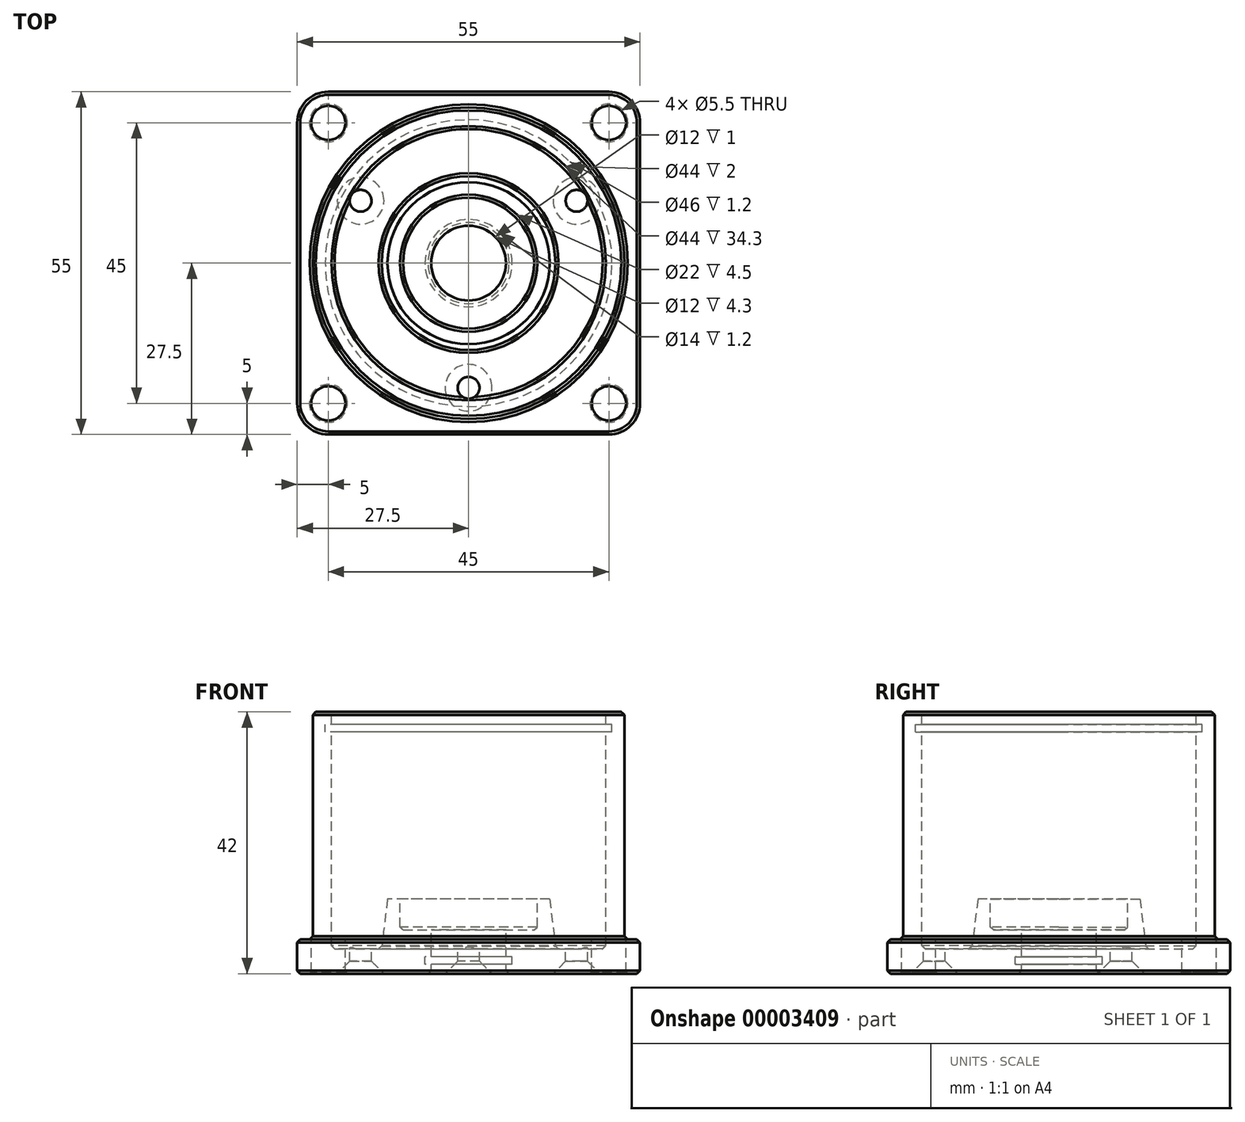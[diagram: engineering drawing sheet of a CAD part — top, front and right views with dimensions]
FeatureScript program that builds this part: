
annotation { "Feature Type Name" : "Feature", "Feature Type Description" : "" }
export const myFeature = defineFeature(function(context is Context, id is Id, definition is map)
    precondition{}
    {
        {
            var Q0;
            Q0=qCreatedBy(makeId("Top.planeOp"),FACE);
            var sketch = newSketch(context, id + "F0", { "sketchPlane" : qUnion([Q0])});
            skLineSegment(sketch, "E0.rect.bottom", {"start": v(-22.5, -27.5) * mm, "end": v(22.5, -27.5) * mm});
            skLineSegment(sketch, "E0.rect.top", {"start": v(-22.5, 27.5) * mm, "end": v(22.5, 27.5) * mm});
            skLineSegment(sketch, "E0.rect.left", {"start": v(-27.5, -22.5) * mm, "end": v(-27.5, 22.5) * mm});
            skLineSegment(sketch, "E0.rect.right", {"start": v(27.5, -22.5) * mm, "end": v(27.5, 22.5) * mm});
            skPoint(sketch, "E0.rect.middle", {"position": v(0, 0) * mm});
            skPoint(sketch, "E1.visualSharp", {"position": v(-27.5, 27.5) * mm});
            skArc(sketch, "E1.filletArc", {"start": v(-22.5, 27.5) * mm, "mid": v(-26.04, 26.04) * mm, "end": v(-27.5, 22.5) * mm});
            skPoint(sketch, "E2.visualSharp", {"position": v(27.5, 27.5) * mm});
            skArc(sketch, "E2.filletArc", {"start": v(27.5, 22.5) * mm, "mid": v(26.04, 26.04) * mm, "end": v(22.5, 27.5) * mm});
            skPoint(sketch, "E3.visualSharp", {"position": v(27.5, -27.5) * mm});
            skArc(sketch, "E3.filletArc", {"start": v(22.5, -27.5) * mm, "mid": v(26.04, -26.04) * mm, "end": v(27.5, -22.5) * mm});
            skPoint(sketch, "E4.visualSharp", {"position": v(-27.5, -27.5) * mm});
            skArc(sketch, "E4.filletArc", {"start": v(-27.5, -22.5) * mm, "mid": v(-26.04, -26.04) * mm, "end": v(-22.5, -27.5) * mm});
            skSolve(sketch);
        }
        {
            var Q0;
            Q0=makeQuery(id+"F0.imprint","IMPRINT",FACE,{"disambiguationData":[TD([[makeQuery(id+"F0.imprint","IMPRINT",EDGE,{"derivedFrom":sQuery(id+"F0.wireOp",EDGE,"E0.rect.bottom")}),1.0]])]});
            extrude(context, id + "F1", {"entities" : qUnion([Q0]), "depth" : 42 * mm});
        }
        {
            var Q0;
            Q0=qCreatedBy(makeId("Right.planeOp"),FACE);
            var sketch = newSketch(context, id + "F2", { "sketchPlane" : qUnion([Q0])});
            skLineSegment(sketch, "E5", {"start": v(-43.6, 5.5) * mm, "end": v(-25, 5.5) * mm});
            skLineSegment(sketch, "E6", {"start": v(-25, 5.5) * mm, "end": v(-25, 44.38) * mm});
            skLineSegment(sketch, "E7", {"start": v(-25, 44.38) * mm, "end": v(-22, 44.38) * mm});
            skLineSegment(sketch, "E8", {"start": v(-22, 44.38) * mm, "end": v(-22, 40) * mm});
            skLineSegment(sketch, "E9", {"start": v(-22, 40) * mm, "end": v(-23, 40) * mm});
            skLineSegment(sketch, "E10", {"start": v(-23, 40) * mm, "end": v(-23, 38.8) * mm});
            skLineSegment(sketch, "E11", {"start": v(-23, 38.8) * mm, "end": v(-22, 38.8) * mm});
            skLineSegment(sketch, "E12", {"start": v(-22, 38.8) * mm, "end": v(-22, 4) * mm});
            skLineSegment(sketch, "E13", {"start": v(-22, 4) * mm, "end": v(-13.98, 4) * mm});
            skLineSegment(sketch, "E14", {"start": v(-13.98, 4) * mm, "end": v(-13, 12) * mm});
            skLineSegment(sketch, "E15", {"start": v(-13, 12) * mm, "end": v(-11, 12) * mm});
            skLineSegment(sketch, "E16", {"start": v(-6, 12) * mm, "end": v(-6, 12) * mm});
            skLineSegment(sketch, "E17", {"start": v(-6, -1.43) * mm, "end": v(0, -1.43) * mm});
            skLineSegment(sketch, "E18", {"start": v(0, -1.43) * mm, "end": v(0, 48.79) * mm});
            skLineSegment(sketch, "E19", {"start": v(0, 48.79) * mm, "end": v(-43.6, 48.79) * mm});
            skLineSegment(sketch, "E20", {"start": v(-43.6, 48.79) * mm, "end": v(-43.6, 5.5) * mm});
            skLineSegment(sketch, "E21", {"start": v(-6, 2.7) * mm, "end": v(-6, 2.7) * mm});
            skLineSegment(sketch, "E22", {"start": v(-7, 2.7) * mm, "end": v(-7, 1.5) * mm});
            skLineSegment(sketch, "E23", {"start": v(-7, 1.5) * mm, "end": v(-6, 1.5) * mm});
            skLineSegment(sketch, "E24", {"start": v(-6, 1.5) * mm, "end": v(-6, -1.43) * mm});
            skLineSegment(sketch, "E25", {"start": v(-6, 2.7) * mm, "end": v(-7, 2.7) * mm});
            skLineSegment(sketch, "E26", {"start": v(-6, 7) * mm, "end": v(-6, 2.7) * mm});
            skLineSegment(sketch, "E27", {"start": v(-11, 12) * mm, "end": v(-11, 7) * mm});
            skLineSegment(sketch, "E28", {"start": v(-11, 7) * mm, "end": v(-6, 7) * mm});
            skSolve(sketch);
        }
        {
            var Q0;
            Q0=makeQuery(id+"F2.imprint","IMPRINT",FACE,{"disambiguationData":[TD([[makeQuery(id+"F2.imprint","IMPRINT",EDGE,{"derivedFrom":sQuery(id+"F2.wireOp",EDGE,"E5")}),1.0]])]});
            var Q1;
            Q1=sQuery(id+"F2.wireOp",EDGE,"E18");
            revolve(context, id + "F3", {"operationType" : NewBodyOperationType.REMOVE, "entities" : qUnion([Q0]), "axis" : qUnion([Q1]), "revolveType" : RevolveType.FULL, "oppositeDirection" : true});
        }
        {
            var Q0;
            Q0=makeQuery(id+"F3.boolean.opBoolean","INTERSECT",EDGE,{"derivedFrom":[makeQuery(id+"F1.opExtrude","CAP_FACE",FACE,{"disambiguationData":[OSD([sQuery(id+"F0.wireOp",EDGE,"E0.rect.bottom"),sQuery(id+"F0.wireOp",EDGE,"E0.rect.top"),sQuery(id+"F0.wireOp",EDGE,"E0.rect.left"),sQuery(id+"F0.wireOp",EDGE,"E0.rect.right"),sQuery(id+"F0.wireOp",EDGE,"E1.filletArc"),sQuery(id+"F0.wireOp",EDGE,"E2.filletArc"),sQuery(id+"F0.wireOp",EDGE,"E3.filletArc"),sQuery(id+"F0.wireOp",EDGE,"E4.filletArc")])],"isStart":true}),makeQuery(id+"F3.opRevolve","SWEPT_FACE",FACE,{"disambiguationData":[OSD([sQuery(id+"F2.wireOp",EDGE,"E24")])]})]});
            var Q1;
            Q1=makeQuery(id+"F1.opExtrude","CAP_FACE",FACE,{"disambiguationData":[OSD([sQuery(id+"F0.wireOp",EDGE,"E0.rect.bottom"),sQuery(id+"F0.wireOp",EDGE,"E0.rect.top"),sQuery(id+"F0.wireOp",EDGE,"E0.rect.left"),sQuery(id+"F0.wireOp",EDGE,"E0.rect.right"),sQuery(id+"F0.wireOp",EDGE,"E1.filletArc"),sQuery(id+"F0.wireOp",EDGE,"E2.filletArc"),sQuery(id+"F0.wireOp",EDGE,"E3.filletArc"),sQuery(id+"F0.wireOp",EDGE,"E4.filletArc")])],"isStart":true});
            var Q2;
            Q2=makeQuery(id+"F3.boolean.opBoolean","COPY",FACE,{"derivedFrom":makeQuery(id+"F3.opRevolve","SWEPT_FACE",FACE,{"disambiguationData":[OSD([sQuery(id+"F2.wireOp",EDGE,"E5")])]})});
            var Q3;
            Q3=makeQuery(id+"F3.boolean.opBoolean","INTERSECT",EDGE,{"derivedFrom":[makeQuery(id+"F1.opExtrude","CAP_FACE",FACE,{"disambiguationData":[OSD([sQuery(id+"F0.wireOp",EDGE,"E0.rect.bottom"),sQuery(id+"F0.wireOp",EDGE,"E0.rect.top"),sQuery(id+"F0.wireOp",EDGE,"E0.rect.left"),sQuery(id+"F0.wireOp",EDGE,"E0.rect.right"),sQuery(id+"F0.wireOp",EDGE,"E1.filletArc"),sQuery(id+"F0.wireOp",EDGE,"E2.filletArc"),sQuery(id+"F0.wireOp",EDGE,"E3.filletArc"),sQuery(id+"F0.wireOp",EDGE,"E4.filletArc")])],"isStart":false}),makeQuery(id+"F3.opRevolve","SWEPT_FACE",FACE,{"disambiguationData":[OSD([sQuery(id+"F2.wireOp",EDGE,"E6")])]})]});
            var Q4;
            Q4=makeQuery(id+"F3.boolean.opBoolean","COPY",EDGE,{"derivedFrom":makeQuery(id+"F3.opRevolve","SWEPT_EDGE",EDGE,{"disambiguationData":[OSD([sQuery(id+"F2.wireOp",EDGE,"E12"),sQuery(id+"F2.wireOp",EDGE,"E13")])]})});
            var Q5;
            Q5=makeQuery(id+"F3.boolean.opBoolean","COPY",EDGE,{"derivedFrom":makeQuery(id+"F3.opRevolve","SWEPT_EDGE",EDGE,{"disambiguationData":[OSD([sQuery(id+"F2.wireOp",EDGE,"E13"),sQuery(id+"F2.wireOp",EDGE,"E14")])]})});
            var Q6;
            Q6=makeQuery(id+"F3.boolean.opBoolean","COPY",EDGE,{"derivedFrom":makeQuery(id+"F3.opRevolve","SWEPT_EDGE",EDGE,{"disambiguationData":[OSD([sQuery(id+"F2.wireOp",EDGE,"E27"),sQuery(id+"F2.wireOp",EDGE,"E28")])]})});
            chamfer(context, id + "F4", {"entities" : qUnion([Q0, Q1, Q2, Q3, Q4, Q5, Q6]), "width" : 0.5 * mm, "tangentPropagation" : true});
        }
        {
            var Q0;
            Q0=makeQuery(id+"F3.boolean.opBoolean","COPY",FACE,{"derivedFrom":makeQuery(id+"F3.opRevolve","SWEPT_FACE",FACE,{"disambiguationData":[OSD([sQuery(id+"F2.wireOp",EDGE,"E5")])]})});
            var sketch = newSketch(context, id + "F5", { "sketchPlane" : qUnion([Q0])});
            skCircle(sketch, "E29", {"center": v(-22.5, 22.5) * mm, "radius": 2.75 * mm});
            skCircle(sketch, "E30", {"center": v(22.5, 22.5) * mm, "radius": 2.75 * mm});
            skCircle(sketch, "E31", {"center": v(22.5, -22.5) * mm, "radius": 2.75 * mm});
            skCircle(sketch, "E32", {"center": v(-22.5, -22.5) * mm, "radius": 2.75 * mm});
            skCircle(sketch, "E33", {"center": v(0, -20) * mm, "radius": 1.75 * mm});
            skSolve(sketch);
        }
        {
            var Q0;
            Q0=makeQuery(id+"F5.imprint","IMPRINT",FACE,{"disambiguationData":[TD([[makeQuery(id+"F5.imprint","IMPRINT",EDGE,{"derivedFrom":sQuery(id+"F5.wireOp",EDGE,"E29")}),1.0]])]});
            var Q1;
            Q1=makeQuery(id+"F5.imprint","IMPRINT",FACE,{"disambiguationData":[TD([[makeQuery(id+"F5.imprint","IMPRINT",EDGE,{"derivedFrom":sQuery(id+"F5.wireOp",EDGE,"E30")}),1.0]])]});
            var Q2;
            Q2=makeQuery(id+"F5.imprint","IMPRINT",FACE,{"disambiguationData":[TD([[makeQuery(id+"F5.imprint","IMPRINT",EDGE,{"derivedFrom":sQuery(id+"F5.wireOp",EDGE,"E31")}),1.0]])]});
            var Q3;
            Q3=makeQuery(id+"F5.imprint","IMPRINT",FACE,{"disambiguationData":[TD([[makeQuery(id+"F5.imprint","IMPRINT",EDGE,{"derivedFrom":sQuery(id+"F5.wireOp",EDGE,"E32")}),1.0]])]});
            extrude(context, id + "F6", {"entities" : qUnion([Q0, Q1, Q2, Q3]), "operationType" : NewBodyOperationType.REMOVE, "oppositeDirection" : true, "depth" : 8 * mm});
        }
        {
            var Q0;
            Q0=makeQuery(id+"F6.boolean.opBoolean","INTERSECT",EDGE,{"derivedFrom":[makeQuery(id+"F1.opExtrude","CAP_FACE",FACE,{"disambiguationData":[OSD([sQuery(id+"F0.wireOp",EDGE,"E0.rect.bottom"),sQuery(id+"F0.wireOp",EDGE,"E0.rect.top"),sQuery(id+"F0.wireOp",EDGE,"E0.rect.left"),sQuery(id+"F0.wireOp",EDGE,"E0.rect.right"),sQuery(id+"F0.wireOp",EDGE,"E1.filletArc"),sQuery(id+"F0.wireOp",EDGE,"E2.filletArc"),sQuery(id+"F0.wireOp",EDGE,"E3.filletArc"),sQuery(id+"F0.wireOp",EDGE,"E4.filletArc")])],"isStart":true}),makeQuery(id+"F6.opExtrude","SWEPT_FACE",FACE,{"disambiguationData":[OSD([sQuery(id+"F5.wireOp",EDGE,"E30")])]})]});
            var Q1;
            Q1=makeQuery(id+"F6.boolean.opBoolean","INTERSECT",EDGE,{"derivedFrom":[makeQuery(id+"F1.opExtrude","CAP_FACE",FACE,{"disambiguationData":[OSD([sQuery(id+"F0.wireOp",EDGE,"E0.rect.bottom"),sQuery(id+"F0.wireOp",EDGE,"E0.rect.top"),sQuery(id+"F0.wireOp",EDGE,"E0.rect.left"),sQuery(id+"F0.wireOp",EDGE,"E0.rect.right"),sQuery(id+"F0.wireOp",EDGE,"E1.filletArc"),sQuery(id+"F0.wireOp",EDGE,"E2.filletArc"),sQuery(id+"F0.wireOp",EDGE,"E3.filletArc"),sQuery(id+"F0.wireOp",EDGE,"E4.filletArc")])],"isStart":true}),makeQuery(id+"F6.opExtrude","SWEPT_FACE",FACE,{"disambiguationData":[OSD([sQuery(id+"F5.wireOp",EDGE,"E29")])]})]});
            var Q2;
            Q2=makeQuery(id+"F6.boolean.opBoolean","INTERSECT",EDGE,{"derivedFrom":[makeQuery(id+"F1.opExtrude","CAP_FACE",FACE,{"disambiguationData":[OSD([sQuery(id+"F0.wireOp",EDGE,"E0.rect.bottom"),sQuery(id+"F0.wireOp",EDGE,"E0.rect.top"),sQuery(id+"F0.wireOp",EDGE,"E0.rect.left"),sQuery(id+"F0.wireOp",EDGE,"E0.rect.right"),sQuery(id+"F0.wireOp",EDGE,"E1.filletArc"),sQuery(id+"F0.wireOp",EDGE,"E2.filletArc"),sQuery(id+"F0.wireOp",EDGE,"E3.filletArc"),sQuery(id+"F0.wireOp",EDGE,"E4.filletArc")])],"isStart":true}),makeQuery(id+"F6.opExtrude","SWEPT_FACE",FACE,{"disambiguationData":[OSD([sQuery(id+"F5.wireOp",EDGE,"E32")])]})]});
            var Q3;
            Q3=makeQuery(id+"F6.boolean.opBoolean","INTERSECT",EDGE,{"derivedFrom":[makeQuery(id+"F1.opExtrude","CAP_FACE",FACE,{"disambiguationData":[OSD([sQuery(id+"F0.wireOp",EDGE,"E0.rect.bottom"),sQuery(id+"F0.wireOp",EDGE,"E0.rect.top"),sQuery(id+"F0.wireOp",EDGE,"E0.rect.left"),sQuery(id+"F0.wireOp",EDGE,"E0.rect.right"),sQuery(id+"F0.wireOp",EDGE,"E1.filletArc"),sQuery(id+"F0.wireOp",EDGE,"E2.filletArc"),sQuery(id+"F0.wireOp",EDGE,"E3.filletArc"),sQuery(id+"F0.wireOp",EDGE,"E4.filletArc")])],"isStart":true}),makeQuery(id+"F6.opExtrude","SWEPT_FACE",FACE,{"disambiguationData":[OSD([sQuery(id+"F5.wireOp",EDGE,"E31")])]})]});
            var Q4;
            Q4=makeQuery(id+"F6.boolean.opBoolean","COPY",EDGE,{"derivedFrom":makeQuery(id+"F6.opExtrude","CAP_EDGE",EDGE,{"disambiguationData":[OSD([sQuery(id+"F5.wireOp",EDGE,"E32")])],"isStart":true})});
            var Q5;
            Q5=makeQuery(id+"F6.boolean.opBoolean","COPY",EDGE,{"derivedFrom":makeQuery(id+"F6.opExtrude","CAP_EDGE",EDGE,{"disambiguationData":[OSD([sQuery(id+"F5.wireOp",EDGE,"E29")])],"isStart":true})});
            var Q6;
            Q6=makeQuery(id+"F6.boolean.opBoolean","COPY",EDGE,{"derivedFrom":makeQuery(id+"F6.opExtrude","CAP_EDGE",EDGE,{"disambiguationData":[OSD([sQuery(id+"F5.wireOp",EDGE,"E30")])],"isStart":true})});
            var Q7;
            Q7=makeQuery(id+"F6.boolean.opBoolean","COPY",EDGE,{"derivedFrom":makeQuery(id+"F6.opExtrude","CAP_EDGE",EDGE,{"disambiguationData":[OSD([sQuery(id+"F5.wireOp",EDGE,"E31")])],"isStart":true})});
            chamfer(context, id + "F7", {"entities" : qUnion([Q0, Q1, Q2, Q3, Q4, Q5, Q6, Q7]), "width" : 0.3 * mm, "tangentPropagation" : true});
        }
        {
            var Q0;
            Q0=makeQuery(id+"F5.imprint","IMPRINT",FACE,{"disambiguationData":[TD([[makeQuery(id+"F5.imprint","IMPRINT",EDGE,{"derivedFrom":sQuery(id+"F5.wireOp",EDGE,"E33")}),1.0]])]});
            extrude(context, id + "F8", {"entities" : qUnion([Q0]), "operationType" : NewBodyOperationType.REMOVE, "oppositeDirection" : true, "depth" : 6 * mm});
        }
        {
            var Q0;
            Q0=makeQuery(id+"F8.boolean.opBoolean","COPY",FACE,{"derivedFrom":makeQuery(id+"F8.opExtrude","SWEPT_FACE",FACE,{"disambiguationData":[OSD([sQuery(id+"F5.wireOp",EDGE,"E33")])]})});
            var Q1;
            Q1=makeQuery(id+"F3.boolean.opBoolean","COPY",FACE,{"derivedFrom":makeQuery(id+"F3.opRevolve","SWEPT_FACE",FACE,{"disambiguationData":[OSD([sQuery(id+"F2.wireOp",EDGE,"E26")])]})});
            circularPattern(context, id + "F9", {"faces" : qUnion([Q0]), "axis" : qUnion([Q1]), "angle" : 120 * degree, "instanceCount" : 3, "patternType" : PatternType.FACE});
        }
        {
            var Q0;
            Q0=makeQuery(id+"F9.opPattern","COPY",EDGE,{"derivedFrom":makeQuery(id+"F8.boolean.opBoolean","INTERSECT",EDGE,{"derivedFrom":[makeQuery(id+"F1.opExtrude","CAP_FACE",FACE,{"disambiguationData":[OSD([sQuery(id+"F0.wireOp",EDGE,"E0.rect.bottom"),sQuery(id+"F0.wireOp",EDGE,"E0.rect.top"),sQuery(id+"F0.wireOp",EDGE,"E0.rect.left"),sQuery(id+"F0.wireOp",EDGE,"E0.rect.right"),sQuery(id+"F0.wireOp",EDGE,"E1.filletArc"),sQuery(id+"F0.wireOp",EDGE,"E2.filletArc"),sQuery(id+"F0.wireOp",EDGE,"E3.filletArc"),sQuery(id+"F0.wireOp",EDGE,"E4.filletArc")])],"isStart":true}),makeQuery(id+"F8.opExtrude","SWEPT_FACE",FACE,{"disambiguationData":[OSD([sQuery(id+"F5.wireOp",EDGE,"E33")])]})]}),"instanceName":"1"});
            var Q1;
            Q1=makeQuery(id+"F9.opPattern","COPY",EDGE,{"derivedFrom":makeQuery(id+"F8.boolean.opBoolean","INTERSECT",EDGE,{"derivedFrom":[makeQuery(id+"F1.opExtrude","CAP_FACE",FACE,{"disambiguationData":[OSD([sQuery(id+"F0.wireOp",EDGE,"E0.rect.bottom"),sQuery(id+"F0.wireOp",EDGE,"E0.rect.top"),sQuery(id+"F0.wireOp",EDGE,"E0.rect.left"),sQuery(id+"F0.wireOp",EDGE,"E0.rect.right"),sQuery(id+"F0.wireOp",EDGE,"E1.filletArc"),sQuery(id+"F0.wireOp",EDGE,"E2.filletArc"),sQuery(id+"F0.wireOp",EDGE,"E3.filletArc"),sQuery(id+"F0.wireOp",EDGE,"E4.filletArc")])],"isStart":true}),makeQuery(id+"F8.opExtrude","SWEPT_FACE",FACE,{"disambiguationData":[OSD([sQuery(id+"F5.wireOp",EDGE,"E33")])]})]}),"instanceName":"2"});
            var Q2;
            Q2=makeQuery(id+"F8.boolean.opBoolean","INTERSECT",EDGE,{"derivedFrom":[makeQuery(id+"F1.opExtrude","CAP_FACE",FACE,{"disambiguationData":[OSD([sQuery(id+"F0.wireOp",EDGE,"E0.rect.bottom"),sQuery(id+"F0.wireOp",EDGE,"E0.rect.top"),sQuery(id+"F0.wireOp",EDGE,"E0.rect.left"),sQuery(id+"F0.wireOp",EDGE,"E0.rect.right"),sQuery(id+"F0.wireOp",EDGE,"E1.filletArc"),sQuery(id+"F0.wireOp",EDGE,"E2.filletArc"),sQuery(id+"F0.wireOp",EDGE,"E3.filletArc"),sQuery(id+"F0.wireOp",EDGE,"E4.filletArc")])],"isStart":true}),makeQuery(id+"F8.opExtrude","SWEPT_FACE",FACE,{"disambiguationData":[OSD([sQuery(id+"F5.wireOp",EDGE,"E33")])]})]});
            chamfer(context, id + "F10", {"entities" : qUnion([Q0, Q1, Q2]), "width" : 2 * mm, "tangentPropagation" : true});
        }
    });
